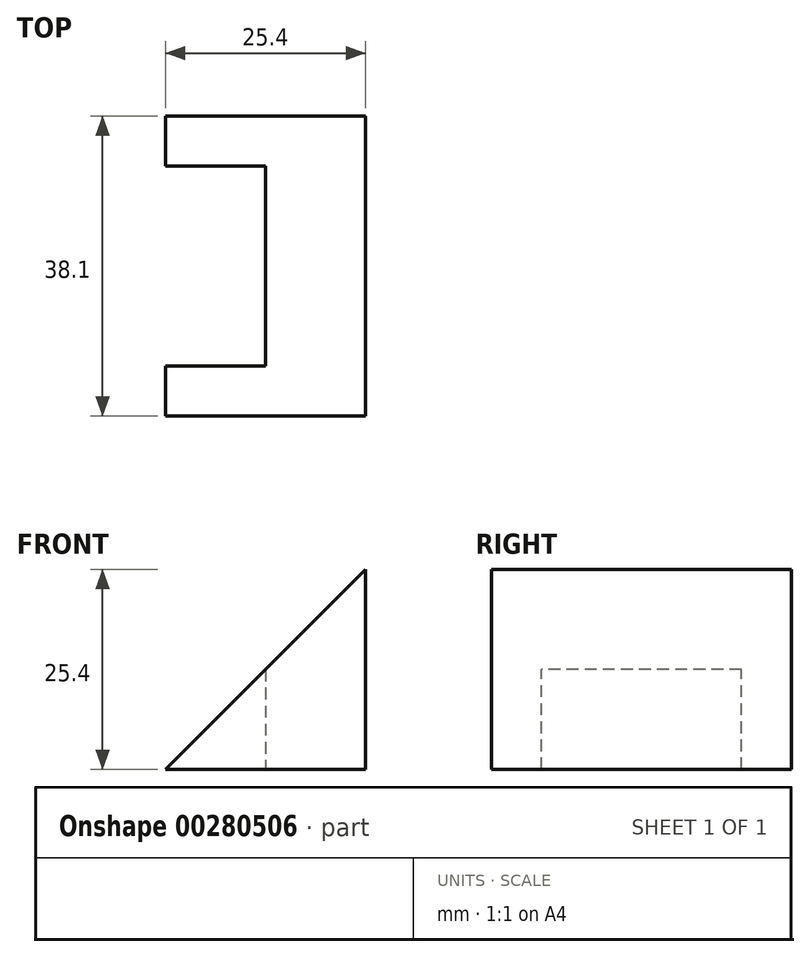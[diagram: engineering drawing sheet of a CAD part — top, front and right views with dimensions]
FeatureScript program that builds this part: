
annotation { "Feature Type Name" : "Feature", "Feature Type Description" : "" }
export const myFeature = defineFeature(function(context is Context, id is Id, definition is map)
    precondition{}
    {
        {
            var Q0;
            Q0=qCreatedBy(makeId("Front.planeOp"),FACE);
            var sketch = newSketch(context, id + "F0", { "sketchPlane" : qUnion([Q0])});
            skLineSegment(sketch, "E0", {"start": v(0, 0) * mm, "end": v(25.4, 25.4) * mm});
            skLineSegment(sketch, "E1", {"start": v(25.4, 25.4) * mm, "end": v(25.4, 0) * mm});
            skLineSegment(sketch, "E2", {"start": v(25.4, 0) * mm, "end": v(0, 0) * mm});
            skSolve(sketch);
        }
        {
            var Q0;
            Q0 = qSketchRegion(id + "F0", true);
            extrude(context, id + "F1", {"entities" : qUnion([Q0]), "depth" : 38.1 * mm});
        }
        {
            var Q0;
            Q0=makeQuery(id+"F1.opExtrude","CAP_FACE",FACE,{"disambiguationData":[OSD([sQuery(id+"F0.wireOp",EDGE,"E0"),sQuery(id+"F0.wireOp",EDGE,"E1"),sQuery(id+"F0.wireOp",EDGE,"E2")])],"isStart":false});
            var sketch = newSketch(context, id + "F2", { "sketchPlane" : qUnion([Q0])});
            skLineSegment(sketch, "E3", {"start": v(12.7, 12.7) * mm, "end": v(12.7, 0) * mm});
            skLineSegment(sketch, "E4", {"start": v(12.7, 0) * mm, "end": v(0, 0) * mm});
            skLineSegment(sketch, "E5", {"start": v(0, 0) * mm, "end": v(12.7, 12.7) * mm});
            skSolve(sketch);
        }
        {
            var Q0;
            Q0 = qSketchRegion(id + "F2", true);
            extrude(context, id + "F3", {"entities" : qUnion([Q0]), "operationType" : NewBodyOperationType.REMOVE, "oppositeDirection" : true, "depth" : 31.75 * mm, "hasSecondDirection" : true, "secondDirectionOppositeDirection" : true, "secondDirectionDepth" : 6.35 * mm});
        }
    });
